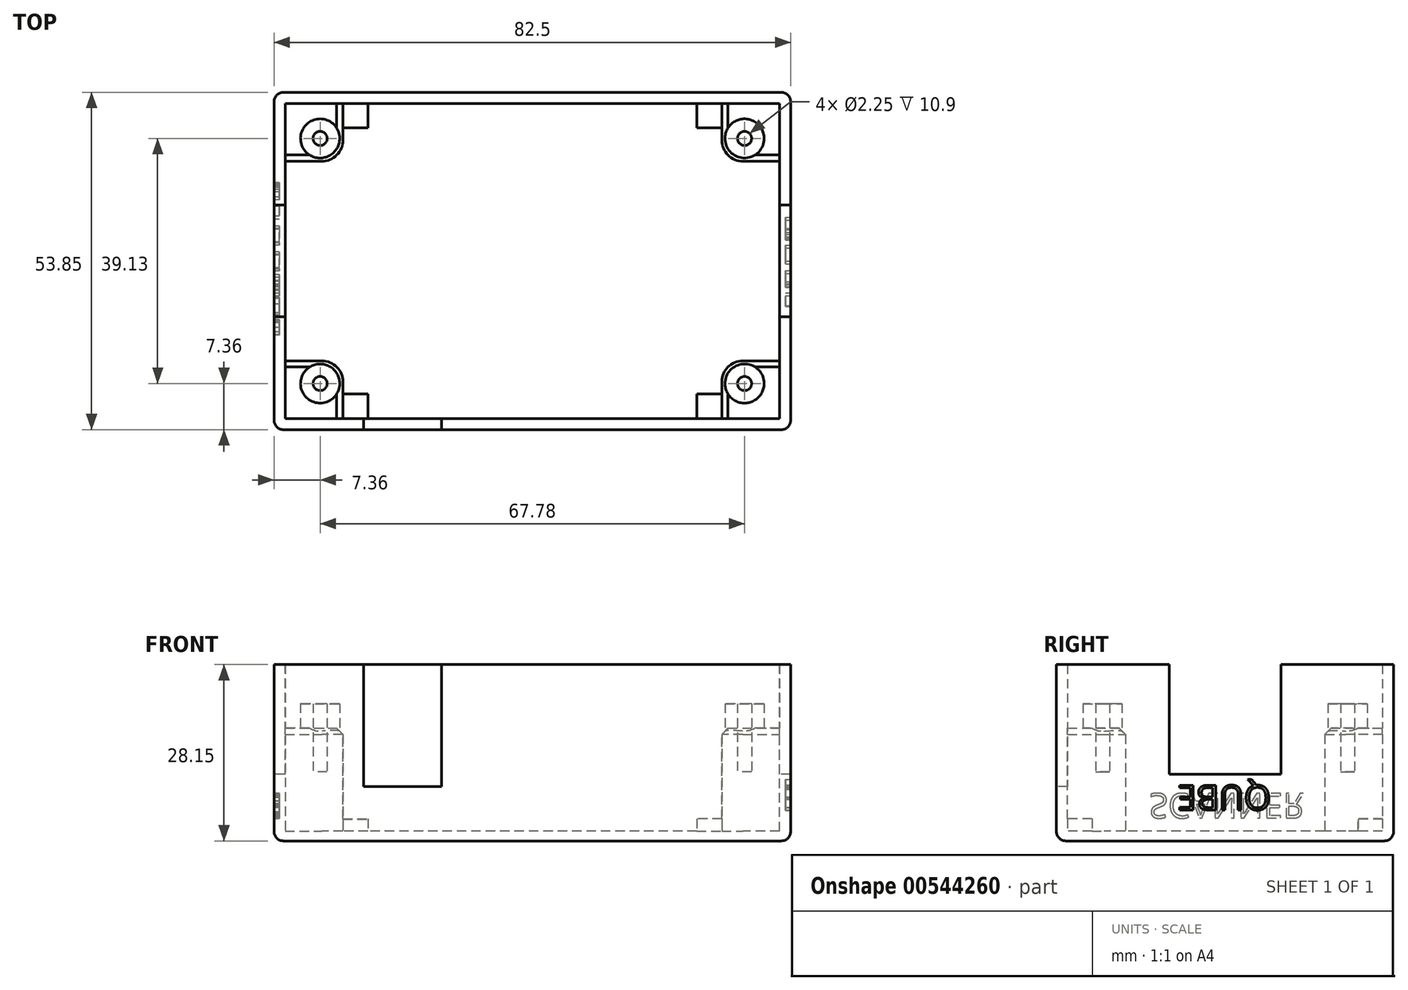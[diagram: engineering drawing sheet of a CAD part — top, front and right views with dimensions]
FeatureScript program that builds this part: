
annotation { "Feature Type Name" : "Feature", "Feature Type Description" : "" }
export const myFeature = defineFeature(function(context is Context, id is Id, definition is map)
    precondition{}
    {
        {
            var Q0;
            Q0=qCreatedBy(makeId("Top.planeOp"),FACE);
            var sketch = newSketch(context, id + "F0", { "sketchPlane" : qUnion([Q0])});
            skLineSegment(sketch, "E0.bottom", {"start": v(0, 0) * mm, "end": v(82.5, 0) * mm});
            skLineSegment(sketch, "E0.top", {"start": v(0, 53.85) * mm, "end": v(82.5, 53.85) * mm});
            skLineSegment(sketch, "E0.left", {"start": v(0, 0) * mm, "end": v(0, 53.85) * mm});
            skLineSegment(sketch, "E0.right", {"start": v(82.5, 0) * mm, "end": v(82.5, 53.85) * mm});
            skLineSegment(sketch, "E1.0", {"start": v(1.78, 1.78) * mm, "end": v(1.78, 52.07) * mm});
            skLineSegment(sketch, "E1.1", {"start": v(1.78, 1.78) * mm, "end": v(80.72, 1.78) * mm});
            skLineSegment(sketch, "E1.2", {"start": v(80.72, 1.78) * mm, "end": v(80.72, 52.07) * mm});
            skLineSegment(sketch, "E1.3", {"start": v(1.78, 52.07) * mm, "end": v(80.72, 52.07) * mm});
            skSolve(sketch);
        }
        {
            var Q0;
            Q0 = qSketchRegion(id + "F0", true);
            extrude(context, id + "F1", {"entities" : qUnion([Q0]), "depth" : 28.15 * mm, "offsetDistance" : 25 * mm});
        }
        {
            var Q0;
            Q0=qCreatedBy(makeId("Front.planeOp"),FACE);
            var sketch = newSketch(context, id + "F2", { "sketchPlane" : qUnion([Q0])});
            skLineSegment(sketch, "E2.bottom", {"start": v(0, 0) * mm, "end": v(82.5, 0) * mm});
            skLineSegment(sketch, "E2.top", {"start": v(0, 1.55) * mm, "end": v(82.5, 1.55) * mm});
            skLineSegment(sketch, "E2.left", {"start": v(0, 0) * mm, "end": v(0, 1.55) * mm});
            skLineSegment(sketch, "E2.right", {"start": v(82.5, 0) * mm, "end": v(82.5, 1.55) * mm});
            skSolve(sketch);
        }
        {
            var Q0;
            Q0 = qSketchRegion(id + "F2", true);
            extrude(context, id + "F3", {"entities" : qUnion([Q0]), "operationType" : NewBodyOperationType.ADD, "depth" : -53.85 * mm, "offsetDistance" : 25 * mm});
        }
        {
            var Q0;
            Q0=qCreatedBy(makeId("Top.planeOp"),FACE);
            var sketch = newSketch(context, id + "F4", { "sketchPlane" : qUnion([Q0])});
            skCircle(sketch, "E3", {"center": v(7.36, 7.36) * mm, "radius": 3.12 * mm});
            skCircle(sketch, "E4", {"center": v(7.36, 46.49) * mm, "radius": 3.12 * mm});
            skCircle(sketch, "E5", {"center": v(75.14, 7.36) * mm, "radius": 3.12 * mm});
            skCircle(sketch, "E6", {"center": v(75.14, 46.49) * mm, "radius": 3.12 * mm});
            skCircle(sketch, "E7.0", {"center": v(7.36, 7.36) * mm, "radius": 1.13 * mm});
            skCircle(sketch, "E8.0", {"center": v(7.36, 46.49) * mm, "radius": 1.13 * mm});
            skCircle(sketch, "E9.0", {"center": v(75.14, 46.49) * mm, "radius": 1.13 * mm});
            skCircle(sketch, "E10.0", {"center": v(75.14, 7.36) * mm, "radius": 1.13 * mm});
            skSolve(sketch);
        }
        {
            var Q0;
            Q0=makeQuery(id+"F4.imprint","IMPRINT",FACE,{"disambiguationData":[TD([[makeQuery(id+"F4.imprint","IMPRINT",EDGE,{"derivedFrom":sQuery(id+"F4.wireOp",EDGE,"E4")}),1.0]])]});
            var Q1;
            Q1=makeQuery(id+"F4.imprint","IMPRINT",FACE,{"disambiguationData":[TD([[makeQuery(id+"F4.imprint","IMPRINT",EDGE,{"derivedFrom":sQuery(id+"F4.wireOp",EDGE,"E3")}),1.0]])]});
            var Q2;
            Q2=makeQuery(id+"F4.imprint","IMPRINT",FACE,{"disambiguationData":[TD([[makeQuery(id+"F4.imprint","IMPRINT",EDGE,{"derivedFrom":sQuery(id+"F4.wireOp",EDGE,"E5")}),1.0]])]});
            var Q3;
            Q3=makeQuery(id+"F4.imprint","IMPRINT",FACE,{"disambiguationData":[TD([[makeQuery(id+"F4.imprint","IMPRINT",EDGE,{"derivedFrom":sQuery(id+"F4.wireOp",EDGE,"E6")}),1.0]])]});
            extrude(context, id + "F5", {"entities" : qUnion([Q0, Q1, Q2, Q3]), "operationType" : NewBodyOperationType.ADD, "depth" : 21.9 * mm, "offsetDistance" : 25 * mm});
        }
        {
            var Q0;
            Q0=qCreatedBy(makeId("Top.planeOp"),FACE);
            var sketch = newSketch(context, id + "F6", { "sketchPlane" : qUnion([Q0])});
            skLineSegment(sketch, "E11.bottom", {"start": v(0, 0) * mm, "end": v(11, 0) * mm});
            skLineSegment(sketch, "E11.left", {"start": v(0, 0) * mm, "end": v(0, 11) * mm});
            skLineSegment(sketch, "E12.top", {"start": v(0, 11) * mm, "end": v(7.62, 11) * mm});
            skLineSegment(sketch, "E12.right", {"start": v(11, 0) * mm, "end": v(11, 7.62) * mm});
            skPoint(sketch, "E13.visualSharp", {"position": v(11, 11) * mm});
            skArc(sketch, "E13.filletArc", {"start": v(11, 7.62) * mm, "mid": v(10.01, 10.01) * mm, "end": v(7.62, 11) * mm});
            skLineSegment(sketch, "E14.direction1", {"start": v(0, 0) * mm, "end": v(11, 0) * mm, "construction": true});
            skLineSegment(sketch, "E14.direction2", {"start": v(0, 0) * mm, "end": v(0, 11) * mm, "construction": true});
            skLineSegment(sketch, "E15.bottom", {"start": v(0, 0) * mm, "end": v(82.5, 0) * mm});
            skLineSegment(sketch, "E15.top", {"start": v(0, 53.85) * mm, "end": v(11, 53.85) * mm});
            skLineSegment(sketch, "E15.left", {"start": v(0, 0) * mm, "end": v(0, 53.85) * mm});
            skLineSegment(sketch, "E15.right", {"start": v(82.5, 0) * mm, "end": v(82.5, 11) * mm});
            skLineSegment(sketch, "E16.0.1.0", {"start": v(11, 53.85) * mm, "end": v(11, 46.23) * mm});
            skLineSegment(sketch, "E16.0.1.1", {"start": v(0, 53.85) * mm, "end": v(11, 53.85) * mm, "construction": true});
            skArc(sketch, "E16.0.1.2", {"start": v(7.62, 42.85) * mm, "mid": v(10.01, 43.84) * mm, "end": v(11, 46.23) * mm});
            skLineSegment(sketch, "E16.0.1.3", {"start": v(0, 53.85) * mm, "end": v(0, 42.85) * mm, "construction": true});
            skPoint(sketch, "E16.0.1.4", {"position": v(11, 42.85) * mm});
            skLineSegment(sketch, "E16.0.1.5", {"start": v(0, 42.85) * mm, "end": v(7.62, 42.85) * mm});
            skLineSegment(sketch, "E16.0.1.7", {"start": v(0, 53.85) * mm, "end": v(0, 42.85) * mm});
            skLineSegment(sketch, "E16.0.1.9", {"start": v(0, 53.85) * mm, "end": v(0, 42.85) * mm});
            skLineSegment(sketch, "E16.1.0.0", {"start": v(71.5, 0) * mm, "end": v(71.5, 7.62) * mm});
            skLineSegment(sketch, "E16.1.0.1", {"start": v(82.5, 0) * mm, "end": v(71.5, 0) * mm, "construction": true});
            skArc(sketch, "E16.1.0.2", {"start": v(74.88, 11) * mm, "mid": v(72.49, 10.01) * mm, "end": v(71.5, 7.62) * mm});
            skLineSegment(sketch, "E16.1.0.3", {"start": v(82.5, 0) * mm, "end": v(82.5, 11) * mm, "construction": true});
            skPoint(sketch, "E16.1.0.4", {"position": v(71.5, 11) * mm});
            skLineSegment(sketch, "E16.1.0.5", {"start": v(82.5, 11) * mm, "end": v(74.88, 11) * mm});
            skLineSegment(sketch, "E16.1.1.0", {"start": v(82.5, 42.85) * mm, "end": v(74.88, 42.85) * mm});
            skLineSegment(sketch, "E16.1.1.1", {"start": v(82.5, 53.85) * mm, "end": v(82.5, 42.85) * mm, "construction": true});
            skArc(sketch, "E16.1.1.2", {"start": v(71.5, 46.23) * mm, "mid": v(72.49, 43.84) * mm, "end": v(74.88, 42.85) * mm});
            skLineSegment(sketch, "E16.1.1.3", {"start": v(82.5, 53.85) * mm, "end": v(71.5, 53.85) * mm, "construction": true});
            skPoint(sketch, "E16.1.1.4", {"position": v(71.5, 42.85) * mm});
            skLineSegment(sketch, "E16.1.1.5", {"start": v(71.5, 53.85) * mm, "end": v(71.5, 46.23) * mm});
            skLineSegment(sketch, "E16.1.1.6", {"start": v(82.5, 53.85) * mm, "end": v(82.5, 42.85) * mm});
            skLineSegment(sketch, "E16.1.1.7", {"start": v(82.5, 53.85) * mm, "end": v(71.5, 53.85) * mm});
            skLineSegment(sketch, "E16.1.1.8", {"start": v(82.5, 53.85) * mm, "end": v(82.5, 42.85) * mm});
            skLineSegment(sketch, "E16.1.1.9", {"start": v(82.5, 53.85) * mm, "end": v(71.5, 53.85) * mm});
            skLineSegment(sketch, "E17.trimOffspring", {"start": v(71.5, 53.85) * mm, "end": v(82.5, 53.85) * mm});
            skLineSegment(sketch, "E18.trimOffspring", {"start": v(0, 42.85) * mm, "end": v(0, 53.85) * mm, "construction": true});
            skLineSegment(sketch, "E19.trimOffspring", {"start": v(71.5, 0) * mm, "end": v(82.5, 0) * mm, "construction": true});
            skLineSegment(sketch, "E20.trimOffspring", {"start": v(82.5, 42.85) * mm, "end": v(82.5, 53.85) * mm});
            skSolve(sketch);
        }
        {
            var Q0;
            Q0 = qSketchRegion(id + "F6", true);
            extrude(context, id + "F7", {"entities" : qUnion([Q0]), "operationType" : NewBodyOperationType.ADD, "depth" : 18 * mm, "offsetDistance" : 25 * mm});
        }
        {
            var Q0;
            Q0=makeQuery(id+"F3.boolean.opBoolean","MERGE",FACE,{"derivedFrom":[makeQuery(id+"F1.opExtrude","CAP_FACE",FACE,{"disambiguationData":[OSD([sQuery(id+"F0.wireOp",EDGE,"E0.bottom"),sQuery(id+"F0.wireOp",EDGE,"E0.top"),sQuery(id+"F0.wireOp",EDGE,"E0.left"),sQuery(id+"F0.wireOp",EDGE,"E0.right"),sQuery(id+"F0.wireOp",EDGE,"E1.0"),sQuery(id+"F0.wireOp",EDGE,"E1.1"),sQuery(id+"F0.wireOp",EDGE,"E1.2"),sQuery(id+"F0.wireOp",EDGE,"E1.3")])],"isStart":true}),makeQuery(id+"F3.opExtrude","SWEPT_FACE",FACE,{"disambiguationData":[OSD([sQuery(id+"F2.wireOp",EDGE,"E2.bottom")])]})]});
            var Q1;
            Q1=makeQuery(id+"F1.opExtrude","SWEPT_EDGE",EDGE,{"disambiguationData":[OSD([sQuery(id+"F0.wireOp",EDGE,"E0.top"),sQuery(id+"F0.wireOp",EDGE,"E0.right")])]});
            var Q2;
            Q2=makeQuery(id+"F1.opExtrude","SWEPT_EDGE",EDGE,{"disambiguationData":[OSD([sQuery(id+"F0.wireOp",EDGE,"E0.bottom"),sQuery(id+"F0.wireOp",EDGE,"E0.right")])]});
            var Q3;
            Q3=makeQuery(id+"F1.opExtrude","SWEPT_EDGE",EDGE,{"disambiguationData":[OSD([sQuery(id+"F0.wireOp",EDGE,"E0.bottom"),sQuery(id+"F0.wireOp",EDGE,"E0.left")])]});
            var Q4;
            Q4=makeQuery(id+"F1.opExtrude","SWEPT_EDGE",EDGE,{"disambiguationData":[OSD([sQuery(id+"F0.wireOp",EDGE,"E0.top"),sQuery(id+"F0.wireOp",EDGE,"E0.left")])]});
            fillet(context, id + "F8", {"entities" : qUnion([Q0, Q1, Q2, Q3, Q4]), "radius" : 1.5 * mm, "tangentPropagation" : true, "allowEdgeOverflow" : false});
        }
        {
            var Q0;
            Q0=makeQuery(id+"F7.opExtrude","CAP_EDGE",EDGE,{"disambiguationData":[OSD([sQuery(id+"F6.wireOp",EDGE,"E16.0.1.0")])],"isStart":false});
            var Q1;
            Q1=makeQuery(id+"F7.opExtrude","CAP_EDGE",EDGE,{"disambiguationData":[OSD([sQuery(id+"F6.wireOp",EDGE,"E16.0.1.5")])],"isStart":false});
            var Q2;
            Q2=makeQuery(id+"F7.opExtrude","CAP_EDGE",EDGE,{"disambiguationData":[OSD([sQuery(id+"F6.wireOp",EDGE,"E12.top")])],"isStart":false});
            var Q3;
            Q3=makeQuery(id+"F7.opExtrude","CAP_EDGE",EDGE,{"disambiguationData":[OSD([sQuery(id+"F6.wireOp",EDGE,"E12.right")])],"isStart":false});
            var Q4;
            Q4=makeQuery(id+"F7.opExtrude","CAP_EDGE",EDGE,{"disambiguationData":[OSD([sQuery(id+"F6.wireOp",EDGE,"E16.1.0.0")])],"isStart":false});
            var Q5;
            Q5=makeQuery(id+"F7.opExtrude","CAP_EDGE",EDGE,{"disambiguationData":[OSD([sQuery(id+"F6.wireOp",EDGE,"E16.1.0.5")])],"isStart":false});
            var Q6;
            Q6=makeQuery(id+"F7.opExtrude","CAP_EDGE",EDGE,{"disambiguationData":[OSD([sQuery(id+"F6.wireOp",EDGE,"E16.1.1.5")])],"isStart":false});
            var Q7;
            Q7=makeQuery(id+"F7.opExtrude","CAP_EDGE",EDGE,{"disambiguationData":[OSD([sQuery(id+"F6.wireOp",EDGE,"E16.1.1.0")])],"isStart":false});
            var Q8;
            Q8=makeQuery(id+"F7.opExtrude","CAP_EDGE",EDGE,{"disambiguationData":[OSD([sQuery(id+"F6.wireOp",EDGE,"E13.filletArc")])],"isStart":false});
            var Q9;
            Q9=makeQuery(id+"F7.opExtrude","CAP_EDGE",EDGE,{"disambiguationData":[OSD([sQuery(id+"F6.wireOp",EDGE,"E16.0.1.2")])],"isStart":false});
            var Q10;
            Q10=makeQuery(id+"F7.opExtrude","CAP_EDGE",EDGE,{"disambiguationData":[OSD([sQuery(id+"F6.wireOp",EDGE,"E16.1.1.2")])],"isStart":false});
            var Q11;
            Q11=makeQuery(id+"F7.opExtrude","CAP_EDGE",EDGE,{"disambiguationData":[OSD([sQuery(id+"F6.wireOp",EDGE,"E16.1.0.2")])],"isStart":false});
            chamfer(context, id + "F9", {"entities" : qUnion([Q0, Q1, Q2, Q3, Q4, Q5, Q6, Q7, Q8, Q9, Q10, Q11]), "width" : 1 * mm});
        }
        {
            var Q0;
            Q0=makeQuery(id+"F7.boolean.opBoolean","SPLIT",FACE,{"disambiguationData":[TD([makeQuery(id+"F5.opExtrude","SWEPT_FACE",FACE,{"disambiguationData":[OSD([sQuery(id+"F4.wireOp",EDGE,"E7.0")])]})])],"derivedFrom":makeQuery(id+"F7.opExtrude","CAP_FACE",FACE,{"disambiguationData":[OSD([sQuery(id+"F6.wireOp",EDGE,"E12.top"),sQuery(id+"F6.wireOp",EDGE,"E12.right"),sQuery(id+"F6.wireOp",EDGE,"E13.filletArc"),sQuery(id+"F6.wireOp",EDGE,"E15.bottom"),sQuery(id+"F6.wireOp",EDGE,"E15.left")])],"isStart":false})});
            var Q1;
            Q1=makeQuery(id+"F7.boolean.opBoolean","SPLIT",FACE,{"disambiguationData":[TD([makeQuery(id+"F5.opExtrude","SWEPT_FACE",FACE,{"disambiguationData":[OSD([sQuery(id+"F4.wireOp",EDGE,"E8.0")])]})])],"derivedFrom":makeQuery(id+"F7.opExtrude","CAP_FACE",FACE,{"disambiguationData":[OSD([sQuery(id+"F6.wireOp",EDGE,"E16.0.1.0"),sQuery(id+"F6.wireOp",EDGE,"E16.0.1.2"),sQuery(id+"F6.wireOp",EDGE,"E16.0.1.5"),sQuery(id+"F6.wireOp",EDGE,"E15.top"),sQuery(id+"F6.wireOp",EDGE,"E16.0.1.9")])],"isStart":false})});
            var Q2;
            Q2=makeQuery(id+"F7.boolean.opBoolean","SPLIT",FACE,{"disambiguationData":[TD([makeQuery(id+"F5.opExtrude","SWEPT_FACE",FACE,{"disambiguationData":[OSD([sQuery(id+"F4.wireOp",EDGE,"E9.0")])]})])],"derivedFrom":makeQuery(id+"F7.opExtrude","CAP_FACE",FACE,{"disambiguationData":[OSD([sQuery(id+"F6.wireOp",EDGE,"E16.1.1.0"),sQuery(id+"F6.wireOp",EDGE,"E16.1.1.2"),sQuery(id+"F6.wireOp",EDGE,"E16.1.1.5"),sQuery(id+"F6.wireOp",EDGE,"E17.trimOffspring"),sQuery(id+"F6.wireOp",EDGE,"E20.trimOffspring")])],"isStart":false})});
            var Q3;
            Q3=makeQuery(id+"F7.boolean.opBoolean","SPLIT",FACE,{"disambiguationData":[TD([makeQuery(id+"F5.opExtrude","SWEPT_FACE",FACE,{"disambiguationData":[OSD([sQuery(id+"F4.wireOp",EDGE,"E10.0")])]})])],"derivedFrom":makeQuery(id+"F7.opExtrude","CAP_FACE",FACE,{"disambiguationData":[OSD([sQuery(id+"F6.wireOp",EDGE,"E15.bottom"),sQuery(id+"F6.wireOp",EDGE,"E16.1.0.0"),sQuery(id+"F6.wireOp",EDGE,"E16.1.0.2"),sQuery(id+"F6.wireOp",EDGE,"E16.1.0.5"),sQuery(id+"F6.wireOp",EDGE,"E15.right")])],"isStart":false})});
            extrude(context, id + "F10", {"entities" : qUnion([Q0, Q1, Q2, Q3]), "operationType" : NewBodyOperationType.REMOVE, "oppositeDirection" : true, "depth" : 7 * mm, "offsetDistance" : 25 * mm});
        }
        {
            var Q0;
            Q0=qCreatedBy(makeId("Right.planeOp"),FACE);
            var sketch = newSketch(context, id + "F11", { "sketchPlane" : qUnion([Q0])});
            skLineSegment(sketch, "E21.bottom", {"start": v(18, 10.65) * mm, "end": v(35.85, 10.65) * mm});
            skLineSegment(sketch, "E21.top", {"start": v(18, 28.15) * mm, "end": v(35.85, 28.15) * mm});
            skLineSegment(sketch, "E21.left", {"start": v(18, 10.65) * mm, "end": v(18, 28.15) * mm});
            skLineSegment(sketch, "E21.right", {"start": v(35.85, 10.65) * mm, "end": v(35.85, 28.15) * mm});
            skSolve(sketch);
        }
        {
            var Q0;
            Q0=makeQuery(id+"F11.imprint","IMPRINT",FACE,{"disambiguationData":[TD([[makeQuery(id+"F11.imprint","IMPRINT",EDGE,{"derivedFrom":sQuery(id+"F11.wireOp",EDGE,"E21.bottom")}),1.0]])]});
            extrude(context, id + "F12", {"entities" : qUnion([Q0]), "operationType" : NewBodyOperationType.REMOVE, "depth" : 137.9 * mm, "offsetDistance" : 25 * mm});
        }
        {
            var Q0;
            Q0=qCreatedBy(makeId("Front.planeOp"),FACE);
            var sketch = newSketch(context, id + "F13", { "sketchPlane" : qUnion([Q0])});
            skLineSegment(sketch, "E22.bottom", {"start": v(14.28, 8.65) * mm, "end": v(26.78, 8.65) * mm});
            skLineSegment(sketch, "E22.top", {"start": v(14.28, 28.15) * mm, "end": v(26.78, 28.15) * mm});
            skLineSegment(sketch, "E22.left", {"start": v(14.28, 8.65) * mm, "end": v(14.28, 28.15) * mm});
            skLineSegment(sketch, "E22.right", {"start": v(26.78, 8.65) * mm, "end": v(26.78, 28.15) * mm});
            skSolve(sketch);
        }
        {
            var Q0;
            Q0 = qSketchRegion(id + "F13", true);
            extrude(context, id + "F14", {"entities" : qUnion([Q0]), "operationType" : NewBodyOperationType.REMOVE, "oppositeDirection" : true, "depth" : 25 * mm, "offsetDistance" : 25 * mm});
        }
        {
            var Q0;
            Q0=makeQuery(id+"F1.opExtrude","SWEPT_FACE",FACE,{"disambiguationData":[OSD([sQuery(id+"F0.wireOp",EDGE,"E0.left")])]});
            var sketch = newSketch(context, id + "F15", { "sketchPlane" : qUnion([Q0])});
            skText(sketch, "E23", { "text": "SCANNER", "fontName": "OpenSans-Regular.ttf"});
            const initialGuessF15  = {"E23": [-0.0148, 0.00757, -1, 0, 0.00396]};
            skSetInitialGuess(sketch, initialGuessF15);
            skSolve(sketch);
        }
        {
            var Q0;
            Q0=makeQuery(id+"F1.opExtrude","SWEPT_FACE",FACE,{"disambiguationData":[OSD([sQuery(id+"F0.wireOp",EDGE,"E0.right")])]});
            var sketch = newSketch(context, id + "F16", { "sketchPlane" : qUnion([Q0])});
            skText(sketch, "E24", { "text": "QUBE", "fontName": "OpenSans-Regular.ttf"});
            const initialGuessF16  = {"E24": [0.03424, 0.00887, -1, 0, 0.00396]};
            skSetInitialGuess(sketch, initialGuessF16);
            skSolve(sketch);
        }
        {
            var Q0;
            Q0 = qSketchRegion(id + "F16", true);
            extrude(context, id + "F17", {"entities" : qUnion([Q0]), "operationType" : NewBodyOperationType.REMOVE, "oppositeDirection" : true, "depth" : .85 * mm, "offsetDistance" : 25 * mm});
        }
        {
            var Q0;
            Q0 = qSketchRegion(id + "F15", true);
            extrude(context, id + "F18", {"entities" : qUnion([Q0]), "operationType" : NewBodyOperationType.REMOVE, "oppositeDirection" : true, "depth" : .85 * mm, "offsetDistance" : 25 * mm});
        }
        {
            var Q0;
            Q0=qCreatedBy(makeId("Right.planeOp"),FACE);
            var sketch = newSketch(context, id + "F19", { "sketchPlane" : qUnion([Q0])});
            skLineSegment(sketch, "E25", {"start": v(48.18, 3.5) * mm, "end": v(52.35, 3.5) * mm});
            skLineSegment(sketch, "E26", {"start": v(52.35, 3.5) * mm, "end": v(52.35, 1.5) * mm});
            skLineSegment(sketch, "E27", {"start": v(52.35, 1.5) * mm, "end": v(48.18, 1.5) * mm});
            skLineSegment(sketch, "E28", {"start": v(48.18, 1.5) * mm, "end": v(48.18, 3.5) * mm});
            skLineSegment(sketch, "E29", {"start": v(5.68, 1.5) * mm, "end": v(1.5, 1.5) * mm});
            skLineSegment(sketch, "E30", {"start": v(1.5, 1.5) * mm, "end": v(1.5, 3.5) * mm});
            skLineSegment(sketch, "E31", {"start": v(1.5, 3.5) * mm, "end": v(5.68, 3.5) * mm});
            skLineSegment(sketch, "E32", {"start": v(5.68, 3.5) * mm, "end": v(5.68, 1.5) * mm});
            skSolve(sketch);
        }
        {
            var Q0;
            Q0 = qSketchRegion(id + "F19", true);
            extrude(context, id + "F20", {"entities" : qUnion([Q0]), "operationType" : NewBodyOperationType.ADD, "depth" : 15 * mm, "offsetDistance" : 25 * mm});
        }
        {
            var Q0;
            {var subQ1=sQuery(id+"F0.wireOp",EDGE,"E0.right");var subQ5=makeQuery(id+"F1.opExtrude","SWEPT_FACE",FACE,{"disambiguationData":[OSD([subQ1])]});Q0=makeQuery(id+"F17.boolean.opBoolean","SPLIT",FACE,{"disambiguationData":[TD([makeQuery(id+"F8.opFillet","BLEND_FACE",FACE,{"disambiguationData":[OSD([subQ1])]})])],"derivedFrom":subQ5});}
            var sketch = newSketch(context, id + "F21", { "sketchPlane" : qUnion([Q0])});
            skLineSegment(sketch, "E33.top", {"start": v(1.5, 3.5) * mm, "end": v(5.67, 3.5) * mm});
            skLineSegment(sketch, "E33.right", {"start": v(5.67, 1.5) * mm, "end": v(5.67, 3.5) * mm});
            skLineSegment(sketch, "E34.top", {"start": v(52.35, 3.5) * mm, "end": v(48.18, 3.5) * mm});
            skLineSegment(sketch, "E34.right", {"start": v(48.17, 1.5) * mm, "end": v(48.17, 3.5) * mm});
            skLineSegment(sketch, "E35", {"start": v(1.5, 3.5) * mm, "end": v(1.5, 1.5) * mm});
            skLineSegment(sketch, "E36", {"start": v(1.5, 1.5) * mm, "end": v(5.67, 1.5) * mm});
            skPoint(sketch, "E33.left.start.orphan", {"position": v(0, 0) * mm});
            skLineSegment(sketch, "E37", {"start": v(52.35, 3.5) * mm, "end": v(52.35, 1.5) * mm});
            skLineSegment(sketch, "E38", {"start": v(52.35, 1.5) * mm, "end": v(48.18, 1.5) * mm});
            skPoint(sketch, "E34.bottom.start.orphan", {"position": v(53.85, 0) * mm});
            skSolve(sketch);
        }
        {
            var Q0;
            Q0 = qSketchRegion(id + "F21", true);
            extrude(context, id + "F22", {"entities" : qUnion([Q0]), "operationType" : NewBodyOperationType.ADD, "depth" : -15 * mm, "offsetDistance" : 25 * mm});
        }
    });
